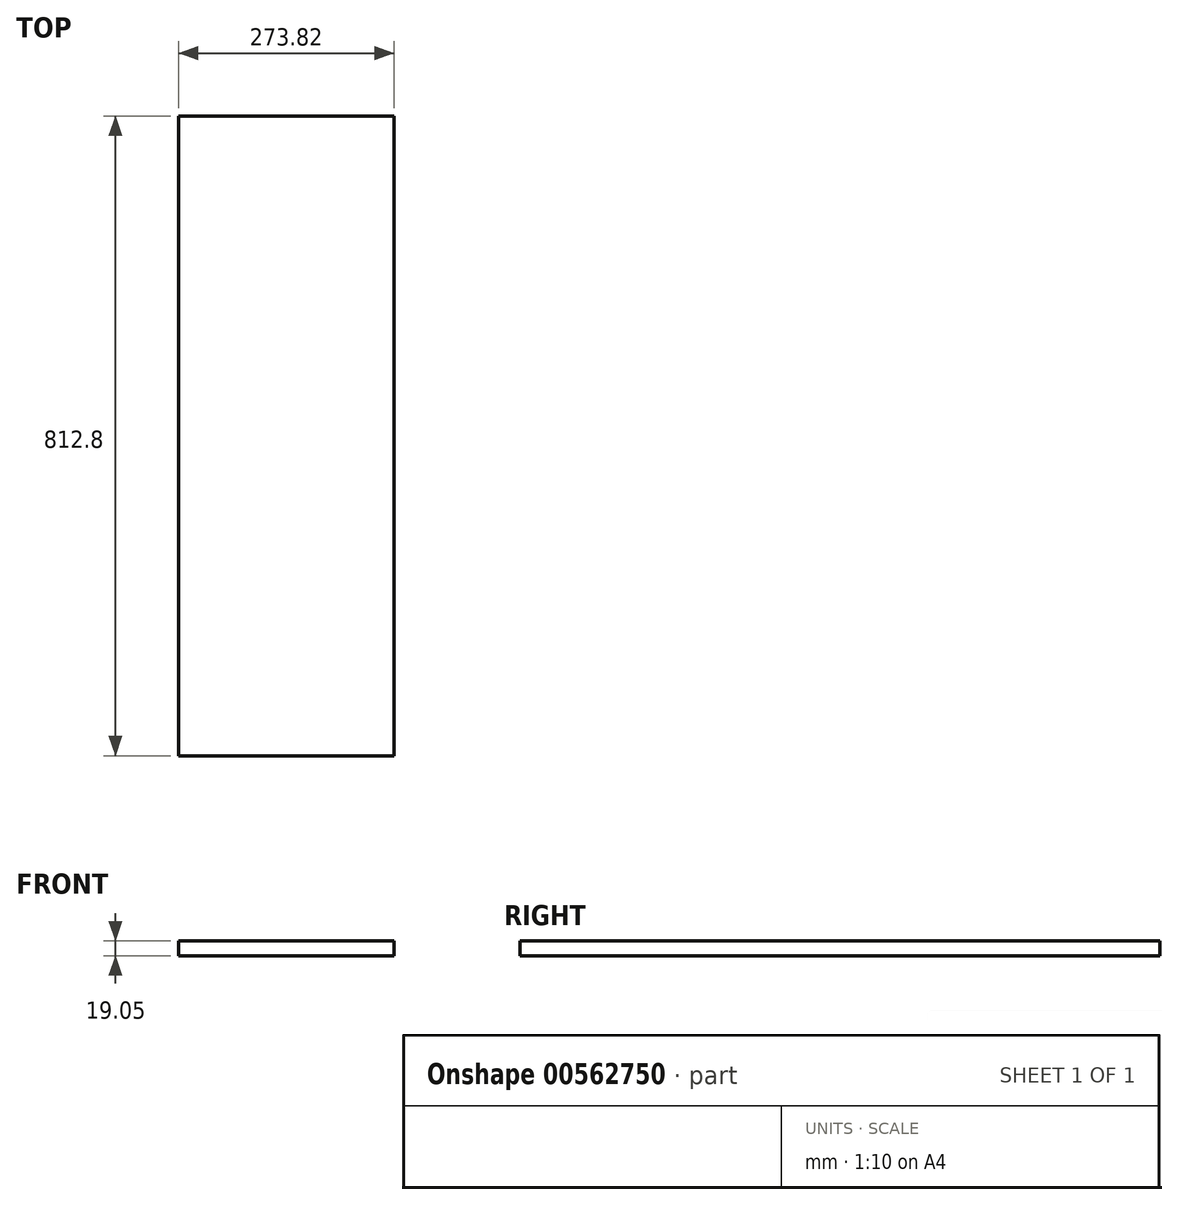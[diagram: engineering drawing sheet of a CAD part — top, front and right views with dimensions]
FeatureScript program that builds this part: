
annotation { "Feature Type Name" : "Feature", "Feature Type Description" : "" }
export const myFeature = defineFeature(function(context is Context, id is Id, definition is map)
    precondition{}
    {
        {
            var Q0;
            Q0=qCreatedBy(makeId("Top.planeOp"),FACE);
            var sketch = newSketch(context, id + "F0", { "sketchPlane" : qUnion([Q0])});
            skLineSegment(sketch, "E0.bottom", {"start": v(136.9, -406.4) * mm, "end": v(-136.9, -406.4) * mm});
            skLineSegment(sketch, "E0.top", {"start": v(136.9, 406.4) * mm, "end": v(-136.9, 406.4) * mm});
            skLineSegment(sketch, "E0.left", {"start": v(136.9, -406.4) * mm, "end": v(136.9, 406.4) * mm});
            skLineSegment(sketch, "E0.right", {"start": v(-136.9, -406.4) * mm, "end": v(-136.9, 406.4) * mm});
            skPoint(sketch, "E0.middle", {"position": v(0, 0) * mm});
            skSolve(sketch);
        }
        {
            var Q0;
            Q0 = qSketchRegion(id + "F0", true);
            extrude(context, id + "F1", {"entities" : qUnion([Q0]), "depth" : 19.05 * mm, "offsetDistance" : 25.4 * mm});
        }
    });
